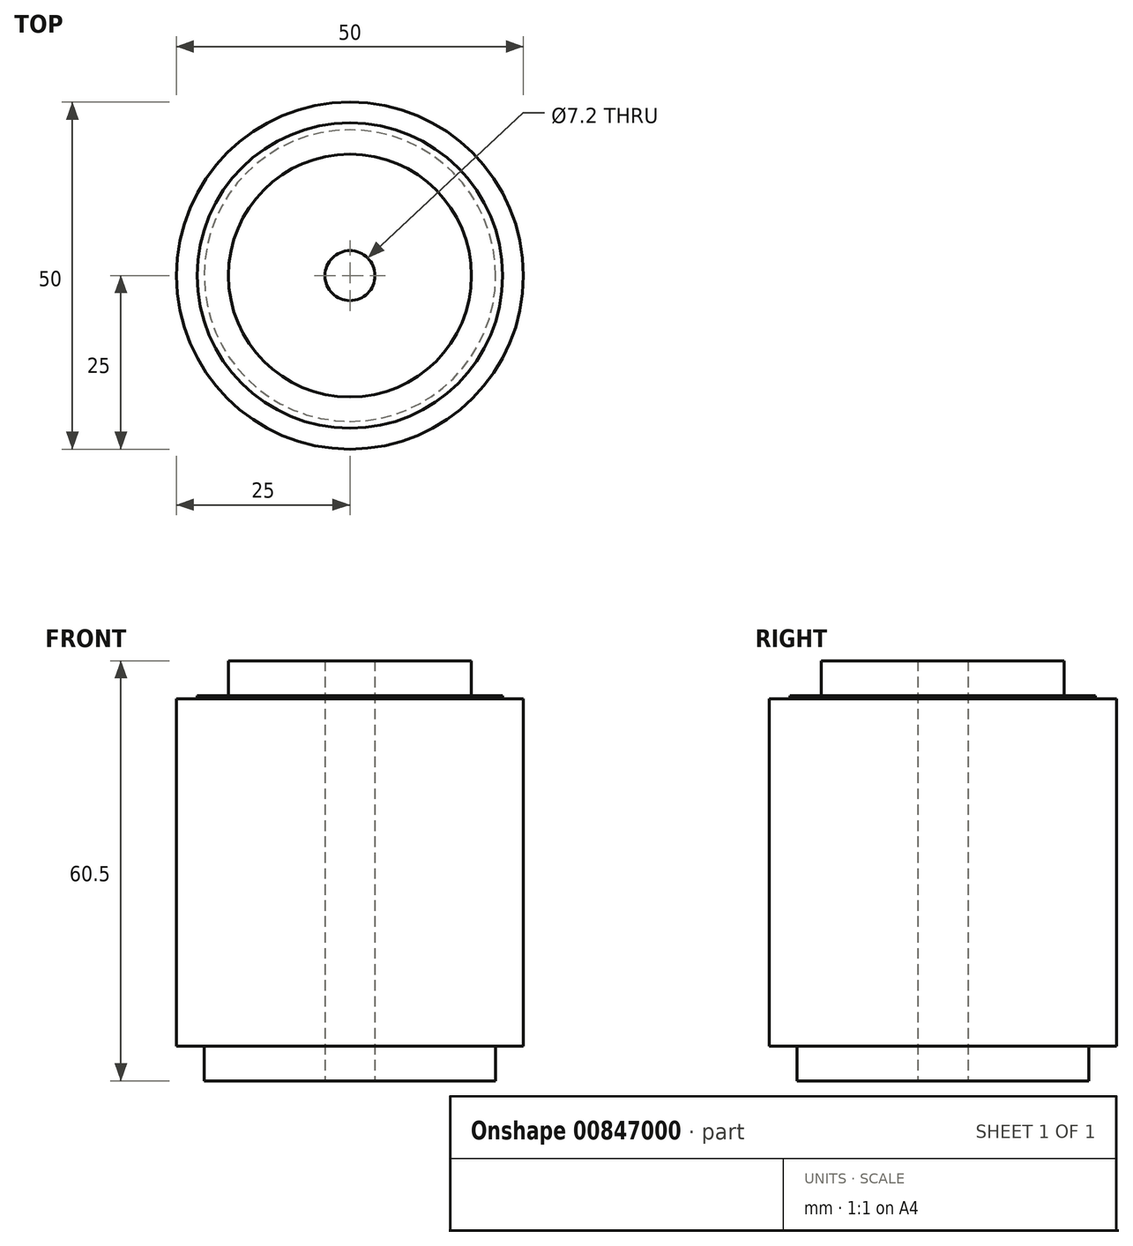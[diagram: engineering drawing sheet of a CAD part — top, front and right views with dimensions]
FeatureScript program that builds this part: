
annotation { "Feature Type Name" : "Feature", "Feature Type Description" : "" }
export const myFeature = defineFeature(function(context is Context, id is Id, definition is map)
    precondition{}
    {
        {
            var Q0;
            Q0=qCreatedBy(makeId("Top.planeOp"),FACE);
            var sketch = newSketch(context, id + "F0", { "sketchPlane" : qUnion([Q0])});
            skCircle(sketch, "E0", {"center": v(0, 0) * mm, "radius": 25 * mm});
            skCircle(sketch, "E1", {"center": v(0, 0) * mm, "radius": 3.6 * mm});
            skSolve(sketch);
        }
        {
            var Q0;
            Q0 = qSketchRegion(id + "F0", true);
            extrude(context, id + "F1", {"entities" : qUnion([Q0]), "depth" : 50 * mm, "offsetDistance" : 25 * mm});
        }
        {
            var Q0;
            Q0=makeQuery(id+"F1.opExtrude","CAP_FACE",FACE,{"disambiguationData":[OSD([sQuery(id+"F0.wireOp",EDGE,"E0"),sQuery(id+"F0.wireOp",EDGE,"E1")])],"isStart":true});
            var sketch = newSketch(context, id + "F2", { "sketchPlane" : qUnion([Q0])});
            skCircle(sketch, "E2", {"center": v(0, 0) * mm, "radius": 21 * mm});
            skSolve(sketch);
        }
        {
            var Q0;
            Q0=makeQuery(id+"F2.imprint","IMPRINT",FACE,{"disambiguationData":[TD([[makeQuery(id+"F2.imprint","IMPRINT",EDGE,{"derivedFrom":sQuery(id+"F2.wireOp",EDGE,"E2")}),1.0]])]});
            extrude(context, id + "F3", {"entities" : qUnion([Q0]), "operationType" : NewBodyOperationType.ADD, "depth" : 5 * mm, "offsetDistance" : 25 * mm});
        }
        {
            var Q0;
            Q0=makeQuery(id+"F1.opExtrude","CAP_FACE",FACE,{"disambiguationData":[OSD([sQuery(id+"F0.wireOp",EDGE,"E0"),sQuery(id+"F0.wireOp",EDGE,"E1")])],"isStart":false});
            var sketch = newSketch(context, id + "F4", { "sketchPlane" : qUnion([Q0])});
            skCircle(sketch, "E3", {"center": v(0, 0) * mm, "radius": 22 * mm});
            skSolve(sketch);
        }
        {
            var Q0;
            Q0=makeQuery(id+"F4.imprint","IMPRINT",FACE,{"disambiguationData":[TD([[makeQuery(id+"F4.imprint","IMPRINT",EDGE,{"derivedFrom":sQuery(id+"F4.wireOp",EDGE,"E3")}),1.0]])]});
            extrude(context, id + "F5", {"entities" : qUnion([Q0]), "operationType" : NewBodyOperationType.ADD, "depth" : .5 * mm, "offsetDistance" : 25 * mm});
        }
        {
            var Q0;
            Q0=makeQuery(id+"F5.opExtrude","CAP_FACE",FACE,{"disambiguationData":[OSD([sQuery(id+"F0.wireOp",EDGE,"E1"),sQuery(id+"F4.wireOp",EDGE,"E3")])],"isStart":false});
            var sketch = newSketch(context, id + "F6", { "sketchPlane" : qUnion([Q0])});
            skCircle(sketch, "E4", {"center": v(0, 0) * mm, "radius": 17.5 * mm});
            skSolve(sketch);
        }
        {
            var Q0;
            Q0=makeQuery(id+"F6.imprint","IMPRINT",FACE,{"disambiguationData":[TD([[makeQuery(id+"F6.imprint","IMPRINT",EDGE,{"derivedFrom":sQuery(id+"F6.wireOp",EDGE,"E4")}),1.0]])]});
            extrude(context, id + "F7", {"entities" : qUnion([Q0]), "operationType" : NewBodyOperationType.ADD, "depth" : 5 * mm, "offsetDistance" : 25 * mm});
        }
    });
